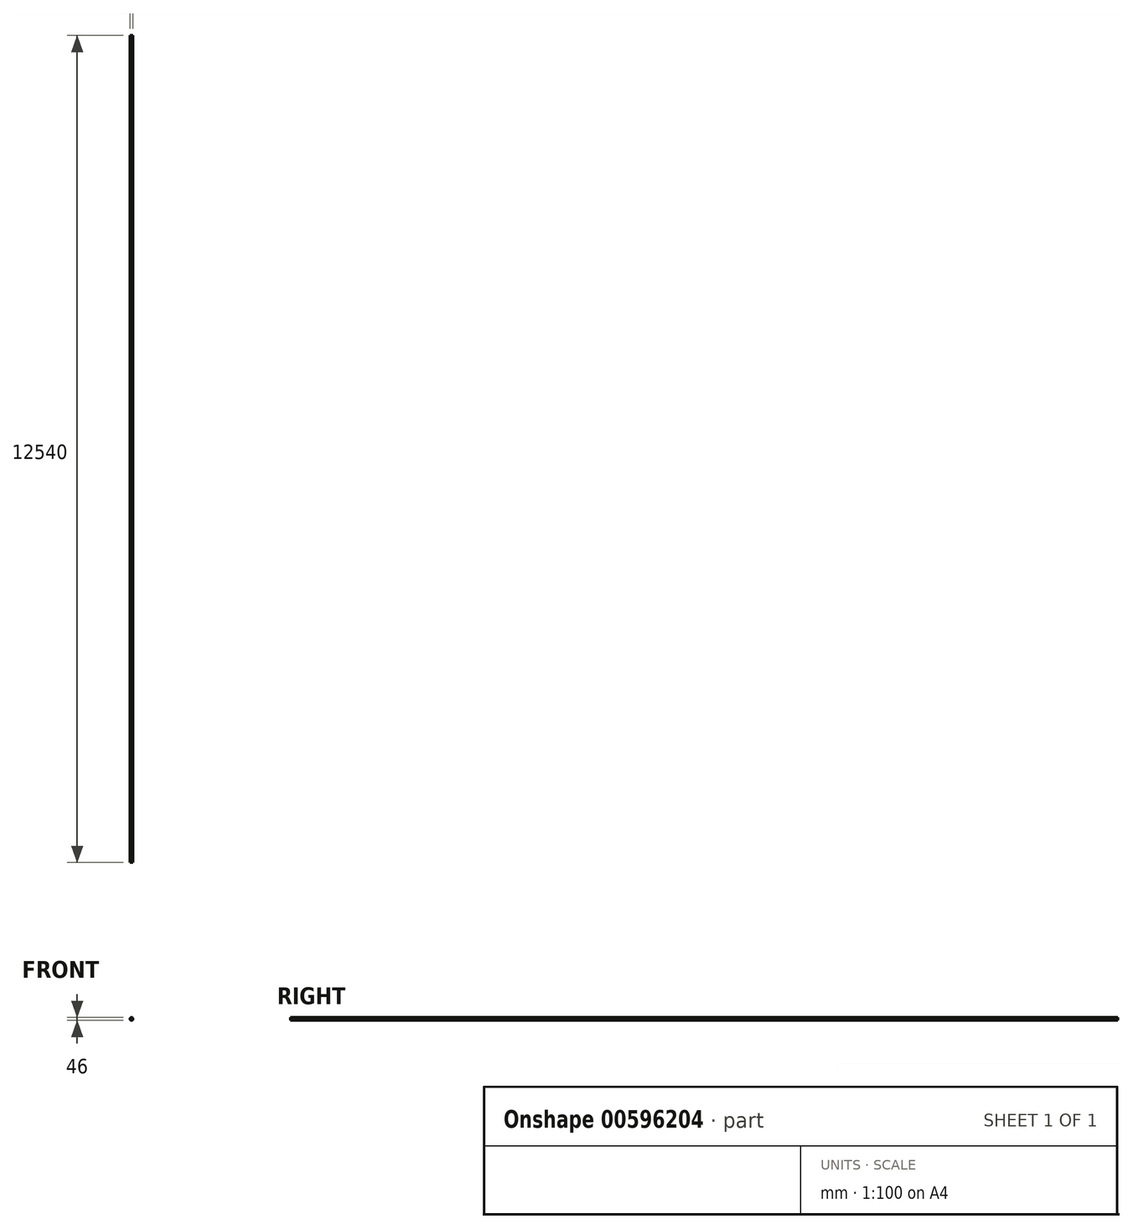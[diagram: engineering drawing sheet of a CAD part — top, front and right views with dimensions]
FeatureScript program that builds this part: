
annotation { "Feature Type Name" : "Feature", "Feature Type Description" : "" }
export const myFeature = defineFeature(function(context is Context, id is Id, definition is map)
    precondition{}
    {
        {
            var Q0;
            Q0=qCreatedBy(makeId("Front.planeOp"),FACE);
            var sketch = newSketch(context, id + "F0", { "sketchPlane" : qUnion([Q0])});
            skCircle(sketch, "E0", {"center": v(113.96, 7.1) * mm, "radius": 23 * mm});
            skSolve(sketch);
        }
        {
            var Q0;
            Q0 = qSketchRegion(id + "F0", true);
            extrude(context, id + "F1", {"entities" : qUnion([Q0]), "oppositeDirection" : true, "depth" : 12540 * mm, "offsetDistance" : 25 * mm});
        }
    });
